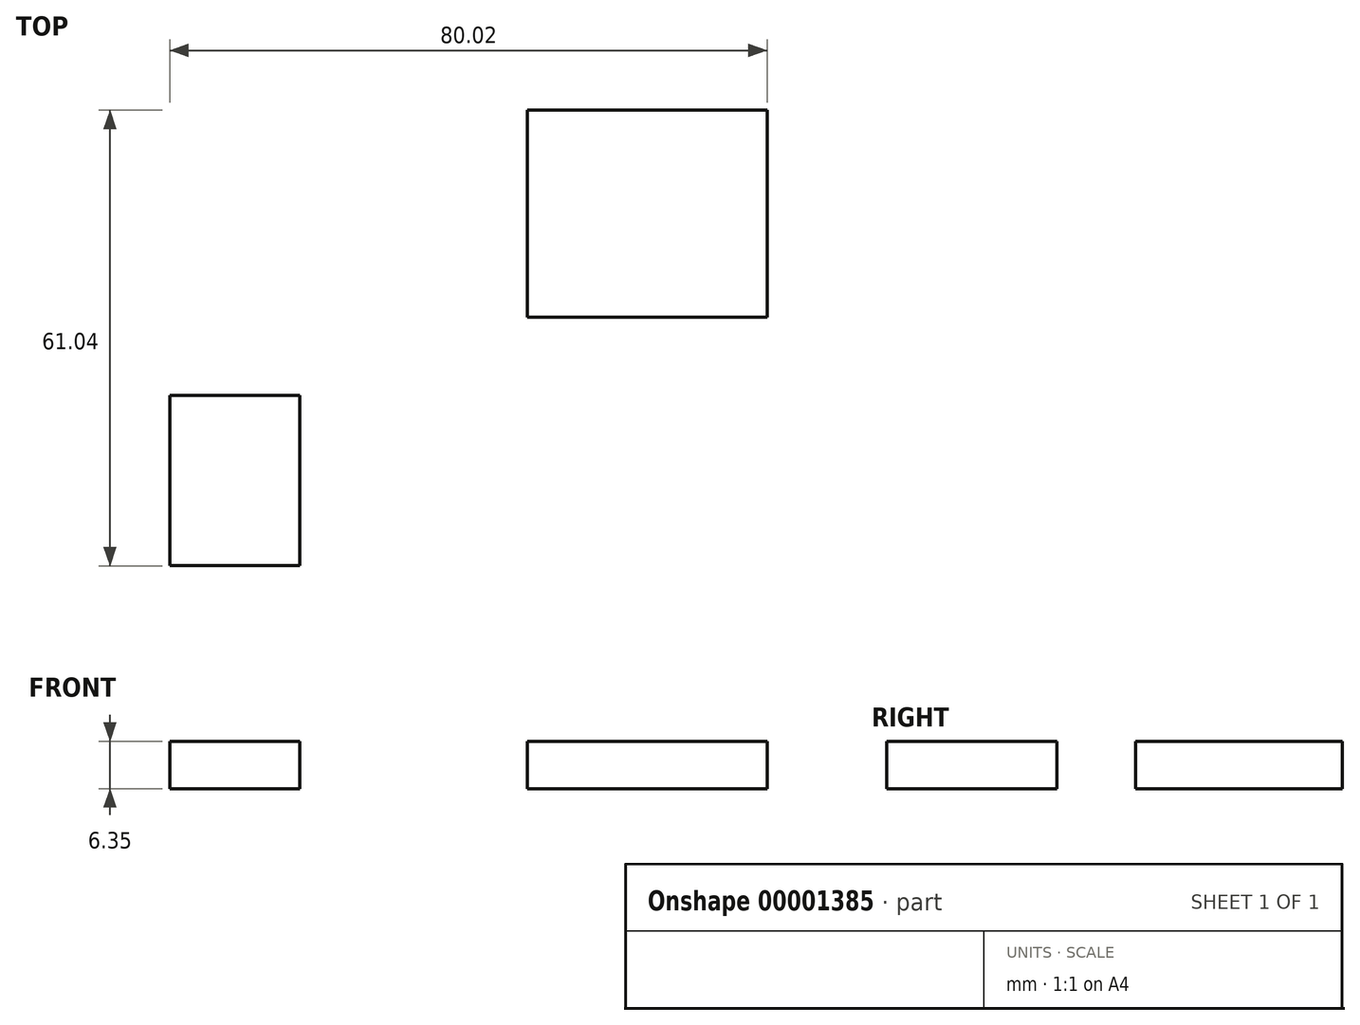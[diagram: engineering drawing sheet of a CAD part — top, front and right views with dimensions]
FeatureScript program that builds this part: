
annotation { "Feature Type Name" : "Feature", "Feature Type Description" : "" }
export const myFeature = defineFeature(function(context is Context, id is Id, definition is map)
    precondition{}
    {
        {
            var Q0;
            Q0=qCreatedBy(makeId("Top.planeOp"),FACE);
            var sketch = newSketch(context, id + "F0", { "sketchPlane" : qUnion([Q0])});
            skLineSegment(sketch, "E0.bottom", {"start": v(0, -22.64) * mm, "end": v(32.12, -22.64) * mm});
            skLineSegment(sketch, "E0.top", {"start": v(0, 5.07) * mm, "end": v(32.12, 5.07) * mm});
            skLineSegment(sketch, "E0.left", {"start": v(0, -22.64) * mm, "end": v(0, 5.07) * mm});
            skLineSegment(sketch, "E0.right", {"start": v(32.12, -22.64) * mm, "end": v(32.12, 5.07) * mm});
            skSolve(sketch);
        }
        {
            var Q0;
            Q0 = qSketchRegion(id + "F0", true);
            extrude(context, id + "F1", {"entities" : qUnion([Q0]), "depth" : 6.35 * mm});
        }
        {
            var Q0;
            Q0=qCreatedBy(makeId("Top.planeOp"),FACE);
            var sketch = newSketch(context, id + "F2", { "sketchPlane" : qUnion([Q0])});
            skLineSegment(sketch, "E1.bottom", {"start": v(-47.9, -33.13) * mm, "end": v(-30.5, -33.13) * mm});
            skLineSegment(sketch, "E1.top", {"start": v(-47.9, -55.97) * mm, "end": v(-30.5, -55.97) * mm});
            skLineSegment(sketch, "E1.left", {"start": v(-47.9, -33.13) * mm, "end": v(-47.9, -55.97) * mm});
            skLineSegment(sketch, "E1.right", {"start": v(-30.5, -33.13) * mm, "end": v(-30.5, -55.97) * mm});
            skSolve(sketch);
        }
        {
            var Q0;
            Q0 = qSketchRegion(id + "F2", true);
            extrude(context, id + "F3", {"entities" : qUnion([Q0]), "depth" : 6.35 * mm});
        }
    });
